# Revit family: Hager-GAMMA-Surface_mounted-IP30-Without_Cover-With_DIN-Hosted-FR-fr
name_source: partatom
category: Electrical Equipment
units: mm (PartAtom-declared; Revit-internal decimal feet)

## family parameters
Cut with Voids When Loaded = No
Host = Face
Maintain Annotation Orientation = Yes
Panel Configuration = Two Columns, Circuits Across
Part Type = Panelboard
Room Calculation Point = No
Round Connector Dimension = Use Diameter
Shared = No

## types (8) — shared parameters
BC_MODEL_ID = 1554287
BC_OBJECT_ID = 513854
BC_OBJECT_VERSION = #3
Code hager = ADD-EC000214_EU
EF000003 - mode de pose = saillie
EF000024 - résistant aux UV = No
EF000049 - profondeur = 103 mm  [stored 0.337927 ft]
EF000118 - avec cadre/support de montage = No
EF001062 - finition CEM = No
EF001088 - possibilité de montage en saillie = No
EF001134 - rail DIN = Yes
EF005474 - indice de protection (IP) = IP30
EF006244 - couvercle/porte transparent(e) = No
EF006306 - avec serrure = No
EF015777 - borne à conducteur neutre = Yes
EF015941 - porte pour transmission du signal = Yes
ETIM class code = EC000214
ETIM class name = Small distribution board
HG000001-nombre de colonnes = 1
HG000002-avec porte = No
HG000003-Gamme = GAMMA
HG000005-Epaisseur = 2 mm  [stored 0.00656168 ft]
HG000006-Encastré = No
HG000009-Porte à double battant = No
HG000010-Portes asymétriques = No
HG000011-Rangées du bas vides = No
HG000012-Angle de pivotement de la porte = 90.00°
HG000013-Porte à gauche = No
HG000014-Porte à droite = Yes
HG000015-Visibilité de l'emprise de la porte = Yes
HG000016-Visibilité de la porte 3D = Yes
HG000017-Distance entre pôles = 18 mm  [stored 0.0590551 ft]
HG000099-ID modèle Onfly = 507532
Manufacturer = Hager
Name = GAMMA-Surface_mounted-IP30-Without_Cover-With_DIN-FR
Name BIM&CO = Electricity
Name hager = ADD_Enclosures_EC000214
Uniformat = Low Tension Service & Dist.
Uniformat code = D501001
zero-valued in all types: Default Elevation, EF000332 - hauteur d'encastrement, EF000846 - largeur d'encastrement, EF001131 - profondeur intérieure, HG000007-Nombre de colonnes vides, HG000008-Nombre de rangées vides

## per-type parameters (varying)
| type | BC_VARIANT_ID | EF000008 - largeur | EF000040 - hauteur | EF000116 - numéro RAL | EF000218 - profondeur d'encastrement | EF000266 - nombre de rangées | EF002950 - largeur en nombre de modules | EF004462 - type de fermeture | EF015776 - borne de mise à la terre | HG000004-Référence fabricant | HG000060-RAL-number | HGEF000266-Nombre de rangées | HGEF0002950-largeur en nombre de modules |
| GAMMA-Surface_mounted_W355_H250_D103_10_Modular_Spacing-GD018E | 1178792 | 355 mm  [stored 1.1647 ft] | 250 mm  [stored 0.82021 ft] | 9010 | 103 mm  [stored 0.337927 ft] | 1 | 10 |  | Yes | GD018E | 9010 | 1 | 10 |
| GAMMA-Surface_mounted_W355_H250_D103_18_Modular_Spacing-GD118A | 1178793 | 355 mm  [stored 1.1647 ft] | 250 mm  [stored 0.82021 ft] | 0 | 0 mm  [stored 0 ft] | 1 | 18 |  | No | GD118A | 0 | 1 | 18 |
| GAMMA-Surface_mounted_W250_H375_D103_13_Modular_Spacing-GD213A | 1178794 | 250 mm  [stored 0.82021 ft] | 375 mm  [stored 1.23031 ft] | 9010 | 0 mm  [stored 0 ft] | 2 | 13 | autre | Yes | GD213A | 9010 | 2 | 13 |
| GAMMA-Surface_mounted_W355_H375_D103_18_Modular_Spacing-GD218A | 1178795 | 355 mm  [stored 1.1647 ft] | 375 mm  [stored 1.23031 ft] | 0 | 0 mm  [stored 0 ft] | 2 | 18 |  | Yes | GD218A | 0 | 2 | 18 |
| GAMMA-Surface_mounted_W250_H500_D103_13_Modular_Spacing-GD313A | 1178796 | 250 mm  [stored 0.82021 ft] | 500 mm  [stored 1.64042 ft] | 9010 | 0 mm  [stored 0 ft] | 3 | 13 | autre | Yes | GD313A | 9010 | 3 | 13 |
| GAMMA-Surface_mounted_W355_H500_D103_18_Modular_Spacing-GD318A | 1178797 | 355 mm  [stored 1.1647 ft] | 500 mm  [stored 1.64042 ft] | 0 | 0 mm  [stored 0 ft] | 3 | 18 |  | No | GD318A | 0 | 3 | 18 |
| GAMMA-Surface_mounted_W250_H625_D103_13_Modular_Spacing-GD413A | 1178798 | 250 mm  [stored 0.82021 ft] | 625 mm  [stored 2.05052 ft] | 9010 | 0 mm  [stored 0 ft] | 4 | 13 | autre | Yes | GD413A | 9010 | 4 | 13 |
| GAMMA-Surface_mounted_W355_H625_D103_18_Modular_Spacing-GD418A | 1178799 | 355 mm  [stored 1.1647 ft] | 625 mm  [stored 2.05052 ft] | 9010 | 0 mm  [stored 0 ft] | 4 | 18 |  | No | GD418A | 9010 | 4 | 18 |

note: column(s) folded — value = type name in every type: Reference

note: [stored X ft] marks values corroborated as IEEE doubles in the binary element streams (Revit-internal decimal feet)

## geometry (parser evidence)
native form markers: Sweep x14
no freeform markers — native parametric forms only
